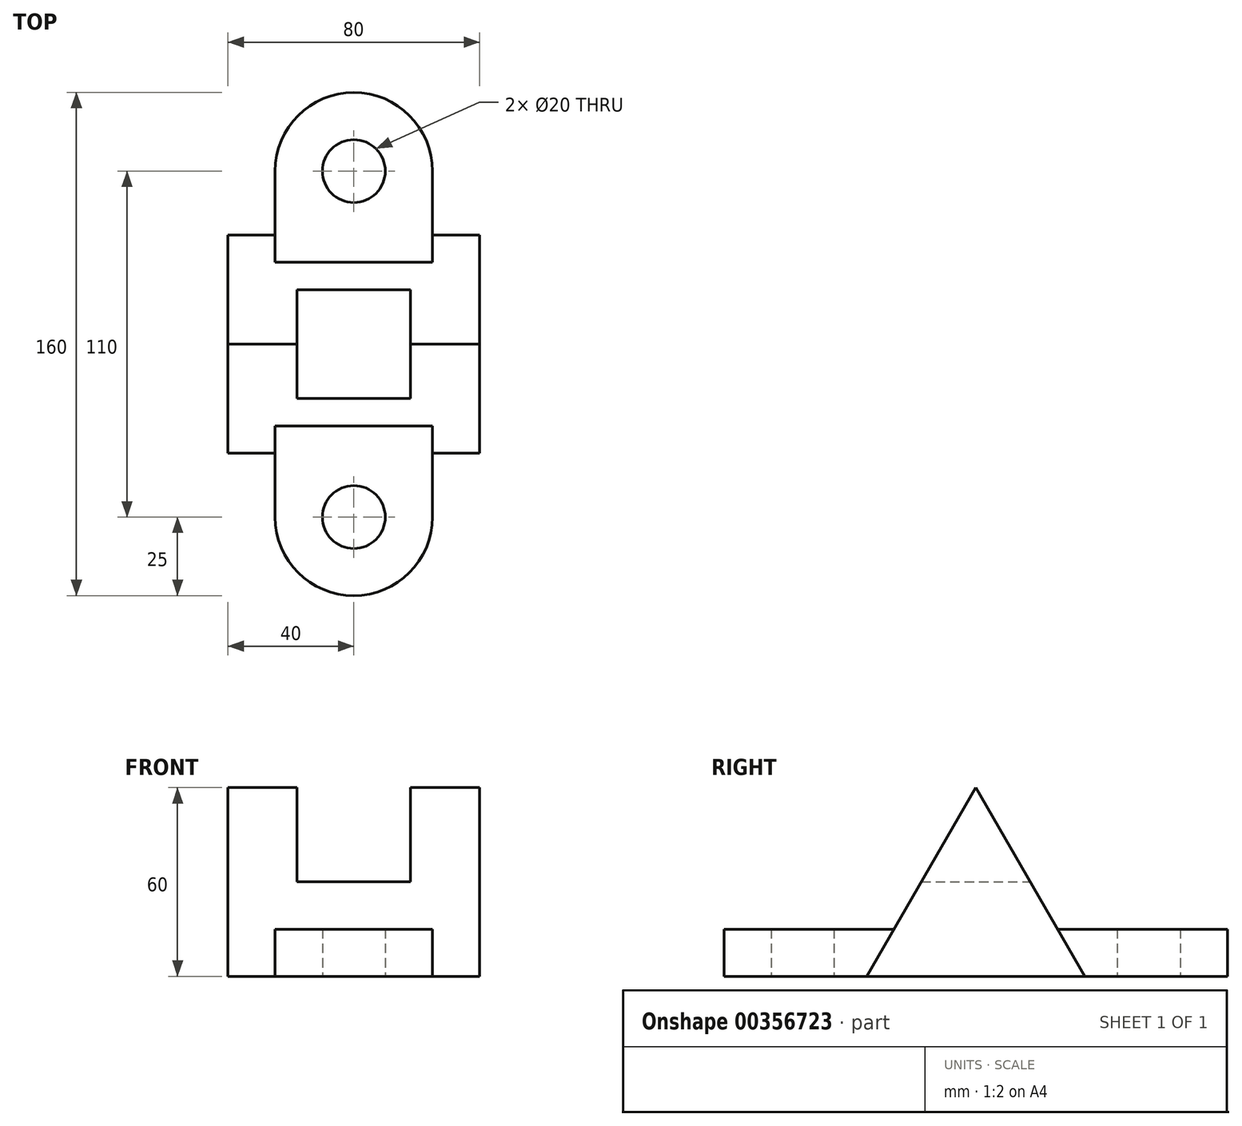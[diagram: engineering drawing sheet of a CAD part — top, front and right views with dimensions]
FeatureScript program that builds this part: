
annotation { "Feature Type Name" : "Feature", "Feature Type Description" : "" }
export const myFeature = defineFeature(function(context is Context, id is Id, definition is map)
    precondition{}
    {
        {
            var Q0;
            Q0=qCreatedBy(makeId("Right.planeOp"),FACE);
            var sketch = newSketch(context, id + "F0", { "sketchPlane" : qUnion([Q0])});
            skLineSegment(sketch, "E0", {"start": v(0, 0) * mm, "end": v(34.64, 0) * mm});
            skLineSegment(sketch, "E1", {"start": v(34.64, 0) * mm, "end": v(0, 60) * mm});
            skLineSegment(sketch, "E2.MirrorCS", {"start": v(-34.64, 0) * mm, "end": v(0, 60) * mm});
            skLineSegment(sketch, "E3.MirrorCS", {"start": v(0, 0) * mm, "end": v(-34.64, 0) * mm});
            skLineSegment(sketch, "E4", {"start": v(0, 0) * mm, "end": v(0, 30) * mm});
            skPoint(sketch, "E5", {"position": v(17.32, 30) * mm});
            skPoint(sketch, "E6", {"position": v(-17.32, 30) * mm});
            skLineSegment(sketch, "E7", {"start": v(-17.32, 30) * mm, "end": v(17.32, 30) * mm});
            skSolve(sketch);
        }
        {
            var Q0;
            {var subQ0=sQuery(id+"F0.wireOp",EDGE,"E0");Q0=makeQuery(id+"F0.imprint","IMPRINT",FACE,{"disambiguationData":[TD([[makeQuery(id+"F0.imprint","IMPRINT",EDGE,{"derivedFrom":subQ0}),1.0]])]});}
            var Q1;
            {var subQ0=sQuery(id+"F0.wireOp",EDGE,"E3.MirrorCS");Q1=makeQuery(id+"F0.imprint","IMPRINT",FACE,{"disambiguationData":[TD([[makeQuery(id+"F0.imprint","IMPRINT",EDGE,{"derivedFrom":subQ0}),-1.0]])]});}
            extrude(context, id + "F1", {"entities" : qUnion([Q0, Q1]), "depth" : 80 * mm});
        }
        {
            var Q0;
            {var subQ0=sQuery(id+"F0.wireOp",EDGE,"E2.MirrorCS");var subQ1=sQuery(id+"F0.wireOp",EDGE,"E1");var subQ2=makeQuery(id+"F0.imprint","INTERSECT",VERTEX,{"derivedFrom":[subQ1,subQ0]});Q0=makeQuery(id+"F0.imprint","IMPRINT",FACE,{"disambiguationData":[TD([[makeQuery(id+"F0.imprint","IMPRINT",EDGE,{"disambiguationData":[TD([[subQ2,1.0]])],"derivedFrom":subQ1}),1.0]])]});}
            extrude(context, id + "F2", {"entities" : qUnion([Q0]), "operationType" : NewBodyOperationType.ADD, "depth" : 22 * mm});
        }
        {
            var Q0;
            {var subQ0=sQuery(id+"F0.wireOp",EDGE,"E7");var subQ1=sQuery(id+"F0.wireOp",EDGE,"E2.MirrorCS");var subQ2=sQuery(id+"F0.wireOp",EDGE,"E1");Q0=makeQuery(id+"F2.boolean.opBoolean","MERGE",FACE,{"derivedFrom":[makeQuery(id+"F1.opExtrude","CAP_FACE",FACE,{"disambiguationData":[OSD([sQuery(id+"F0.wireOp",EDGE,"E0"),subQ2,subQ1,sQuery(id+"F0.wireOp",EDGE,"E3.MirrorCS"),subQ0])],"isStart":true}),makeQuery(id+"F2.opExtrude","CAP_FACE",FACE,{"disambiguationData":[OSD([subQ2,subQ1,subQ0])],"isStart":true})]});}
            var sketch = newSketch(context, id + "F3", { "sketchPlane" : qUnion([Q0])});
            skPoint(sketch, "E8.0", {"position": v(0, 60) * mm});
            skPoint(sketch, "E9.0", {"position": v(17.32, 30) * mm});
            skPoint(sketch, "E10.0", {"position": v(-17.32, 30) * mm});
            skLineSegment(sketch, "E11", {"start": v(-17.32, 30) * mm, "end": v(17.32, 30) * mm});
            skSolve(sketch);
        }
        {
            var Q0;
            Q0=makeQuery(id+"F1.opExtrude","CAP_FACE",FACE,{"disambiguationData":[OSD([sQuery(id+"F0.wireOp",EDGE,"E0"),sQuery(id+"F0.wireOp",EDGE,"E1"),sQuery(id+"F0.wireOp",EDGE,"E2.MirrorCS"),sQuery(id+"F0.wireOp",EDGE,"E3.MirrorCS"),sQuery(id+"F0.wireOp",EDGE,"E7")])],"isStart":false});
            var sketch = newSketch(context, id + "F4", { "sketchPlane" : qUnion([Q0])});
            skPoint(sketch, "E12.0", {"position": v(17.32, 30) * mm});
            skPoint(sketch, "E12.1", {"position": v(-17.32, 30) * mm});
            skPoint(sketch, "E13.0", {"position": v(0, 60) * mm});
            skLineSegment(sketch, "E14", {"start": v(-17.32, 30) * mm, "end": v(0, 60) * mm});
            skLineSegment(sketch, "E15", {"start": v(17.32, 30) * mm, "end": v(0, 60) * mm});
            skSolve(sketch);
        }
        {
            var Q0;
            Q0=makeQuery(id+"F4.imprint","IMPRINT",FACE,{"disambiguationData":[TD([[makeQuery(id+"F4.imprint","IMPRINT",EDGE,{"derivedFrom":sQuery(id+"F4.wireOp",EDGE,"E14")}),-1.0]])]});
            extrude(context, id + "F5", {"entities" : qUnion([Q0]), "operationType" : NewBodyOperationType.ADD, "depth" : -22 * mm});
        }
        {
            var Q0;
            {var subQ0=sQuery(id+"F0.wireOp",EDGE,"E2.MirrorCS");Q0=makeQuery(id+"F5.boolean.opBoolean","MERGE",FACE,{"derivedFrom":[makeQuery(id+"F2.boolean.opBoolean","MERGE",FACE,{"derivedFrom":[makeQuery(id+"F1.opExtrude","SWEPT_FACE",FACE,{"disambiguationData":[OSD([subQ0])]}),makeQuery(id+"F2.opExtrude","SWEPT_FACE",FACE,{"disambiguationData":[OSD([subQ0])]})]}),makeQuery(id+"F5.opExtrude","SWEPT_FACE",FACE,{"disambiguationData":[OSD([sQuery(id+"F4.wireOp",EDGE,"E14")])]})]});}
            var sketch = newSketch(context, id + "F6", { "sketchPlane" : qUnion([Q0])});
            skSolve(sketch);
        }
        {
            var Q0;
            Q0=qCreatedBy(makeId("Top.planeOp"),FACE);
            var sketch = newSketch(context, id + "F7", { "sketchPlane" : qUnion([Q0])});
            skCircle(sketch, "E16", {"center": v(40, 55) * mm, "radius": 10 * mm});
            skArc(sketch, "E17", {"start": v(65, 55) * mm, "mid": v(40, 80) * mm, "end": v(15, 55) * mm});
            skArc(sketch, "E18.MirrorC", {"start": v(65, -55) * mm, "mid": v(40, -80) * mm, "end": v(15, -55) * mm});
            skCircle(sketch, "E19.MirrorC", {"center": v(40, -55) * mm, "radius": 10 * mm});
            skLineSegment(sketch, "E20", {"start": v(15, 55) * mm, "end": v(15, -55) * mm});
            skLineSegment(sketch, "E21", {"start": v(65, 55) * mm, "end": v(65, -55) * mm});
            skSolve(sketch);
        }
        {
            var Q0;
            Q0=makeQuery(id+"F7.imprint","IMPRINT",FACE,{"disambiguationData":[TD([[makeQuery(id+"F7.imprint","IMPRINT",EDGE,{"derivedFrom":sQuery(id+"F7.wireOp",EDGE,"E16")}),-1.0]])]});
            extrude(context, id + "F8", {"entities" : qUnion([Q0]), "operationType" : NewBodyOperationType.ADD, "depth" : 15 * mm});
        }
    });
